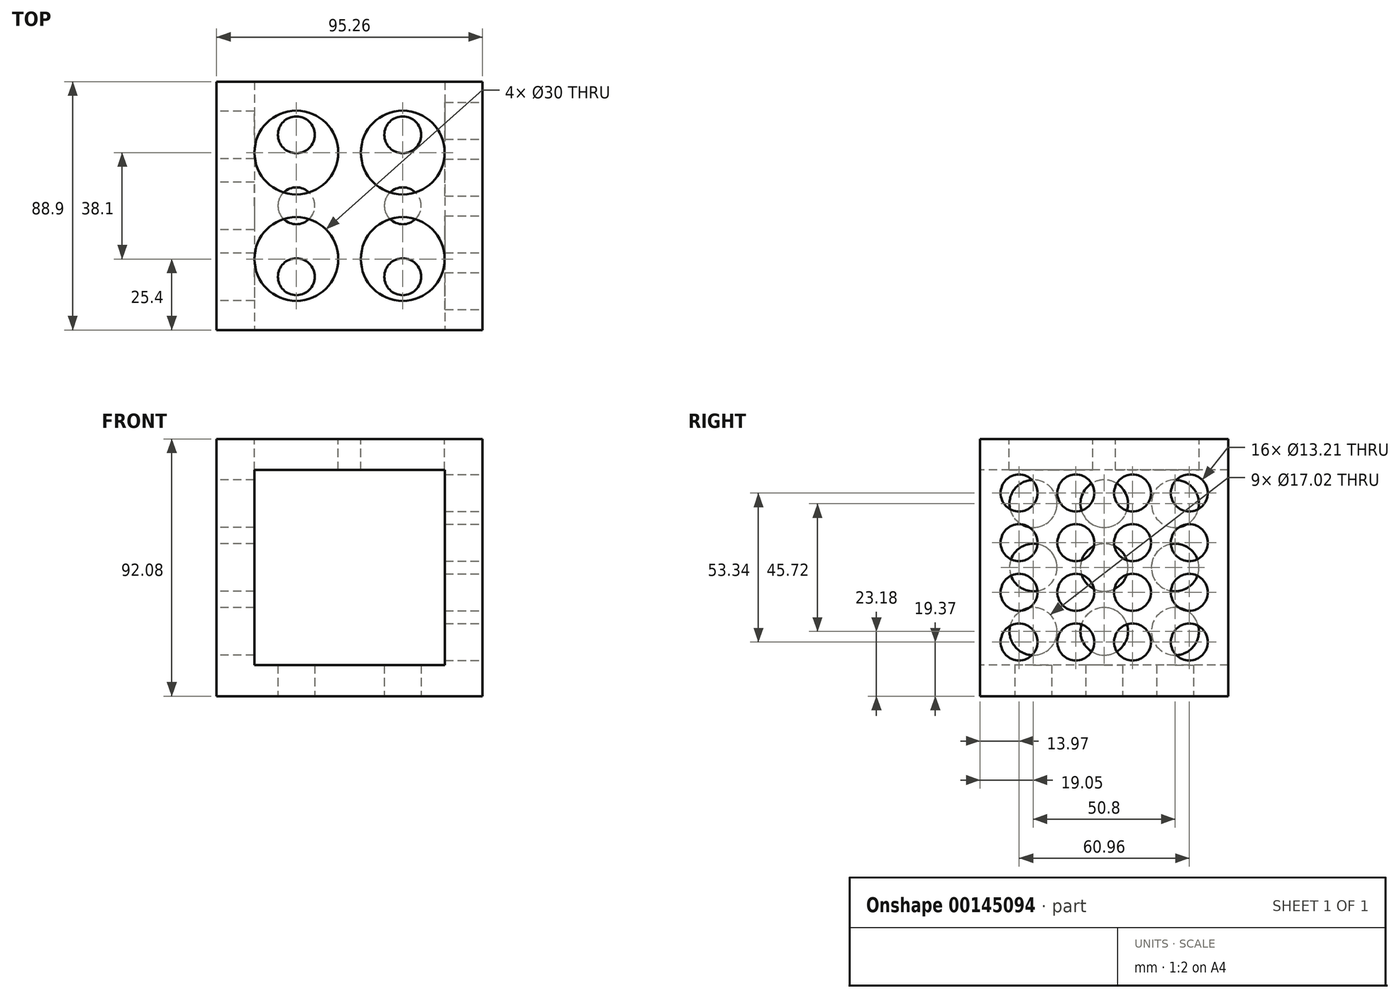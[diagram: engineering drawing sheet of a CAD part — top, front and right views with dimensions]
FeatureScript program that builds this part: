
annotation { "Feature Type Name" : "Feature", "Feature Type Description" : "" }
export const myFeature = defineFeature(function(context is Context, id is Id, definition is map)
    precondition{}
    {
        {
            var Q0;
            Q0=qCreatedBy(makeId("Top.planeOp"),FACE);
            var sketch = newSketch(context, id + "F0", { "sketchPlane" : qUnion([Q0])});
            skLineSegment(sketch, "E0.bottom", {"start": v(47.63, -44.45) * mm, "end": v(-47.62, -44.45) * mm});
            skLineSegment(sketch, "E0.top", {"start": v(47.63, 44.45) * mm, "end": v(-47.62, 44.45) * mm});
            skLineSegment(sketch, "E0.left", {"start": v(47.63, -44.45) * mm, "end": v(47.63, 44.45) * mm});
            skLineSegment(sketch, "E0.right", {"start": v(-47.62, -44.45) * mm, "end": v(-47.62, 44.45) * mm});
            skPoint(sketch, "E0.middle", {"position": v(0, 0) * mm});
            skSolve(sketch);
        }
        {
            var Q0;
            Q0=makeQuery(id+"F0.imprint","IMPRINT",FACE,{"disambiguationData":[TD([[makeQuery(id+"F0.imprint","IMPRINT",EDGE,{"derivedFrom":sQuery(id+"F0.wireOp",EDGE,"E0.bottom")}),-1.0]])]});
            extrude(context, id + "F1", {"entities" : qUnion([Q0]), "depth" : 46.04 * mm, "hasSecondDirection" : true, "secondDirectionOppositeDirection" : true, "secondDirectionDepth" : 46.04 * mm});
        }
        {
            var Q0;
            Q0=makeQuery(id+"F1.opExtrude","SWEPT_FACE",FACE,{"disambiguationData":[OSD([sQuery(id+"F0.wireOp",EDGE,"E0.bottom")])]});
            var sketch = newSketch(context, id + "F2", { "sketchPlane" : qUnion([Q0])});
            skLineSegment(sketch, "E1.bottom", {"start": v(34.13, -34.93) * mm, "end": v(-34.13, -34.93) * mm});
            skLineSegment(sketch, "E1.top", {"start": v(34.13, 34.93) * mm, "end": v(-34.13, 34.92) * mm});
            skLineSegment(sketch, "E1.left", {"start": v(34.13, -34.93) * mm, "end": v(34.13, 34.93) * mm});
            skLineSegment(sketch, "E1.right", {"start": v(-34.13, -34.93) * mm, "end": v(-34.13, 34.92) * mm});
            skPoint(sketch, "E1.middle", {"position": v(0, 0) * mm});
            skLineSegment(sketch, "E2.bottom", {"start": v(1.59, -34.93) * mm, "end": v(-1.59, -34.93) * mm});
            skLineSegment(sketch, "E2.top", {"start": v(1.59, 34.93) * mm, "end": v(-1.59, 34.93) * mm});
            skLineSegment(sketch, "E2.left", {"start": v(1.59, -34.92) * mm, "end": v(1.59, 34.92) * mm});
            skLineSegment(sketch, "E2.right", {"start": v(-1.59, -34.92) * mm, "end": v(-1.59, 34.92) * mm});
            skSolve(sketch);
        }
        {
            var Q0;
            Q0=makeQuery(id+"F2.imprint","IMPRINT",FACE,{"disambiguationData":[TD([[makeQuery(id+"F2.imprint","IMPRINT",EDGE,{"derivedFrom":sQuery(id+"F2.wireOp",EDGE,"E1.bottom")}),-1.0]])]});
            extrude(context, id + "F3", {"entities" : qUnion([Q0]), "operationType" : NewBodyOperationType.REMOVE, "endBound" : BoundingType.UP_TO_NEXT, "oppositeDirection" : true, "depth" : 25.4 * mm});
        }
        {
            var Q0;
            Q0=makeQuery(id+"F1.opExtrude","CAP_FACE",FACE,{"disambiguationData":[OSD([sQuery(id+"F0.wireOp",EDGE,"E0.bottom"),sQuery(id+"F0.wireOp",EDGE,"E0.top"),sQuery(id+"F0.wireOp",EDGE,"E0.left"),sQuery(id+"F0.wireOp",EDGE,"E0.right")])],"isStart":false});
            var sketch = newSketch(context, id + "F4", { "sketchPlane" : qUnion([Q0])});
            skLineSegment(sketch, "E3", {"start": v(0, 0) * mm, "end": v(-19.05, 0) * mm});
            skLineSegment(sketch, "E4", {"start": v(-19.05, 0) * mm, "end": v(-19.05, 19.05) * mm});
            skCircle(sketch, "E5", {"center": v(-19.05, 19.05) * mm, "radius": 15 * mm});
            skLineSegment(sketch, "E6", {"start": v(0, 0) * mm, "end": v(19.05, 0) * mm});
            skLineSegment(sketch, "E7", {"start": v(19.05, 0) * mm, "end": v(19.05, 19.05) * mm});
            skLineSegment(sketch, "E8", {"start": v(-19.05, 0) * mm, "end": v(-19.05, -19.05) * mm});
            skLineSegment(sketch, "E9", {"start": v(19.05, 0) * mm, "end": v(19.05, -19.05) * mm});
            skCircle(sketch, "E10", {"center": v(19.05, 19.05) * mm, "radius": 15 * mm});
            skCircle(sketch, "E11", {"center": v(19.05, -19.05) * mm, "radius": 15 * mm});
            skCircle(sketch, "E12", {"center": v(-19.05, -19.05) * mm, "radius": 15 * mm});
            skSolve(sketch);
        }
        {
            var Q0;
            Q0=makeQuery(id+"F4.imprint","IMPRINT",FACE,{"disambiguationData":[TD([[makeQuery(id+"F4.imprint","IMPRINT",EDGE,{"derivedFrom":sQuery(id+"F4.wireOp",EDGE,"E5")}),1.0]])]});
            var Q1;
            Q1=makeQuery(id+"F4.imprint","IMPRINT",FACE,{"disambiguationData":[TD([[makeQuery(id+"F4.imprint","IMPRINT",EDGE,{"derivedFrom":sQuery(id+"F4.wireOp",EDGE,"E10")}),1.0]])]});
            var Q2;
            Q2=makeQuery(id+"F4.imprint","IMPRINT",FACE,{"disambiguationData":[TD([[makeQuery(id+"F4.imprint","IMPRINT",EDGE,{"derivedFrom":sQuery(id+"F4.wireOp",EDGE,"E11")}),1.0]])]});
            var Q3;
            Q3=makeQuery(id+"F4.imprint","IMPRINT",FACE,{"disambiguationData":[TD([[makeQuery(id+"F4.imprint","IMPRINT",EDGE,{"derivedFrom":sQuery(id+"F4.wireOp",EDGE,"E12")}),1.0]])]});
            extrude(context, id + "F5", {"entities" : qUnion([Q0, Q1, Q2, Q3]), "operationType" : NewBodyOperationType.REMOVE, "endBound" : BoundingType.UP_TO_NEXT, "oppositeDirection" : true, "depth" : 25.4 * mm});
        }
        {
            var Q0;
            Q0=makeQuery(id+"F1.opExtrude","SWEPT_FACE",FACE,{"disambiguationData":[OSD([sQuery(id+"F0.wireOp",EDGE,"E0.right")])]});
            var sketch = newSketch(context, id + "F6", { "sketchPlane" : qUnion([Q0])});
            skCircle(sketch, "E13", {"center": v(0, 0) * mm, "radius": 8.5 * mm});
            skLineSegment(sketch, "E14", {"start": v(0, 0) * mm, "end": v(0, 22.86) * mm});
            skLineSegment(sketch, "E15", {"start": v(0, 0) * mm, "end": v(0, -22.86) * mm});
            skCircle(sketch, "E16", {"center": v(0, 22.86) * mm, "radius": 8.5 * mm});
            skCircle(sketch, "E17", {"center": v(0, -22.86) * mm, "radius": 8.5 * mm});
            skCircle(sketch, "E18.1.0.0", {"center": v(-25.4, 22.86) * mm, "radius": 8.5 * mm});
            skCircle(sketch, "E18.1.0.1", {"center": v(-25.4, 0) * mm, "radius": 8.5 * mm});
            skCircle(sketch, "E18.1.0.2", {"center": v(-25.4, -22.86) * mm, "radius": 8.5 * mm});
            skLineSegment(sketch, "E18.direction1", {"start": v(0, 22.86) * mm, "end": v(-25.4, 22.86) * mm, "construction": true});
            skCircle(sketch, "E19.1.0.0", {"center": v(25.4, 22.86) * mm, "radius": 8.5 * mm});
            skCircle(sketch, "E19.1.0.1", {"center": v(25.4, 0) * mm, "radius": 8.5 * mm});
            skCircle(sketch, "E19.1.0.2", {"center": v(25.4, -22.86) * mm, "radius": 8.5 * mm});
            skLineSegment(sketch, "E19.direction1", {"start": v(0, 22.86) * mm, "end": v(25.4, 22.86) * mm, "construction": true});
            skSolve(sketch);
        }
        {
            var Q0;
            Q0 = qSketchRegion(id + "F6", true);
            extrude(context, id + "F7", {"entities" : qUnion([Q0]), "operationType" : NewBodyOperationType.REMOVE, "endBound" : BoundingType.UP_TO_NEXT, "oppositeDirection" : true, "depth" : 25.4 * mm});
        }
        {
            var Q0;
            Q0=makeQuery(id+"F1.opExtrude","CAP_FACE",FACE,{"disambiguationData":[OSD([sQuery(id+"F0.wireOp",EDGE,"E0.bottom"),sQuery(id+"F0.wireOp",EDGE,"E0.top"),sQuery(id+"F0.wireOp",EDGE,"E0.left"),sQuery(id+"F0.wireOp",EDGE,"E0.right")])],"isStart":true});
            var sketch = newSketch(context, id + "F8", { "sketchPlane" : qUnion([Q0])});
            skLineSegment(sketch, "E20", {"start": v(0, 0) * mm, "end": v(-19.05, 0) * mm});
            skPoint(sketch, "E20.endSnap0", {"position": v(-47.62, 0) * mm});
            skCircle(sketch, "E21", {"center": v(-19.05, 0) * mm, "radius": 6.6 * mm});
            skLineSegment(sketch, "E22", {"start": v(-19.05, 0) * mm, "end": v(-19.05, 25.4) * mm});
            skLineSegment(sketch, "E23", {"start": v(-19.05, 0) * mm, "end": v(-19.05, -25.4) * mm});
            skCircle(sketch, "E24", {"center": v(-19.05, 25.4) * mm, "radius": 6.6 * mm});
            skCircle(sketch, "E25", {"center": v(-19.05, -25.4) * mm, "radius": 6.6 * mm});
            skCircle(sketch, "E26.1.0.0", {"center": v(19.05, 25.4) * mm, "radius": 6.6 * mm});
            skLineSegment(sketch, "E26.1.0.1", {"start": v(19.05, 0) * mm, "end": v(19.05, 25.4) * mm});
            skCircle(sketch, "E26.1.0.2", {"center": v(19.05, 0) * mm, "radius": 6.6 * mm});
            skCircle(sketch, "E26.1.0.3", {"center": v(19.05, -25.4) * mm, "radius": 6.6 * mm});
            skLineSegment(sketch, "E26.direction1", {"start": v(-19.05, 25.4) * mm, "end": v(19.05, 25.4) * mm, "construction": true});
            skSolve(sketch);
        }
        {
            var Q0;
            Q0 = qSketchRegion(id + "F8", true);
            extrude(context, id + "F9", {"entities" : qUnion([Q0]), "operationType" : NewBodyOperationType.REMOVE, "endBound" : BoundingType.UP_TO_NEXT, "oppositeDirection" : true, "depth" : 25.4 * mm});
        }
        {
            var Q0;
            Q0=makeQuery(id+"F1.opExtrude","SWEPT_FACE",FACE,{"disambiguationData":[OSD([sQuery(id+"F0.wireOp",EDGE,"E0.left")])]});
            var sketch = newSketch(context, id + "F10", { "sketchPlane" : qUnion([Q0])});
            skLineSegment(sketch, "E27", {"start": v(0, 0) * mm, "end": v(-30.48, 0) * mm});
            skLineSegment(sketch, "E28", {"start": v(-30.48, 0) * mm, "end": v(-30.48, 8.89) * mm});
            skLineSegment(sketch, "E29", {"start": v(-30.48, 8.89) * mm, "end": v(-30.48, 26.67) * mm});
            skCircle(sketch, "E30", {"center": v(-30.48, 8.89) * mm, "radius": 6.6 * mm});
            skCircle(sketch, "E31", {"center": v(-30.48, 26.67) * mm, "radius": 6.6 * mm});
            skCircle(sketch, "E32.MirrorC", {"center": v(-30.48, -8.89) * mm, "radius": 6.6 * mm});
            skLineSegment(sketch, "E33.MirrorCS", {"start": v(-30.48, -8.89) * mm, "end": v(-30.48, -26.67) * mm});
            skLineSegment(sketch, "E34.MirrorCS", {"start": v(-30.48, 0) * mm, "end": v(-30.48, -8.89) * mm});
            skCircle(sketch, "E35.MirrorC", {"center": v(-30.48, -26.67) * mm, "radius": 6.6 * mm});
            skCircle(sketch, "E36.1.0.0", {"center": v(-10.16, 26.67) * mm, "radius": 6.6 * mm});
            skLineSegment(sketch, "E36.1.0.1", {"start": v(-10.16, 8.89) * mm, "end": v(-10.16, 26.67) * mm});
            skCircle(sketch, "E36.1.0.2", {"center": v(-10.16, 8.89) * mm, "radius": 6.6 * mm});
            skLineSegment(sketch, "E36.1.0.3", {"start": v(-10.16, 0) * mm, "end": v(-10.16, -8.89) * mm});
            skLineSegment(sketch, "E36.1.0.4", {"start": v(-10.16, 0) * mm, "end": v(-10.16, 8.89) * mm});
            skCircle(sketch, "E36.1.0.5", {"center": v(-10.16, -8.89) * mm, "radius": 6.6 * mm});
            skLineSegment(sketch, "E36.1.0.6", {"start": v(-10.16, -8.89) * mm, "end": v(-10.16, -26.67) * mm});
            skCircle(sketch, "E36.1.0.7", {"center": v(-10.16, -26.67) * mm, "radius": 6.6 * mm});
            skCircle(sketch, "E36.2.0.0", {"center": v(10.16, 26.67) * mm, "radius": 6.6 * mm});
            skLineSegment(sketch, "E36.2.0.1", {"start": v(10.16, 8.89) * mm, "end": v(10.16, 26.67) * mm});
            skCircle(sketch, "E36.2.0.2", {"center": v(10.16, 8.89) * mm, "radius": 6.6 * mm});
            skLineSegment(sketch, "E36.2.0.3", {"start": v(10.16, 0) * mm, "end": v(10.16, -8.89) * mm});
            skLineSegment(sketch, "E36.2.0.4", {"start": v(10.16, 0) * mm, "end": v(10.16, 8.89) * mm});
            skCircle(sketch, "E36.2.0.5", {"center": v(10.16, -8.89) * mm, "radius": 6.6 * mm});
            skLineSegment(sketch, "E36.2.0.6", {"start": v(10.16, -8.89) * mm, "end": v(10.16, -26.67) * mm});
            skCircle(sketch, "E36.2.0.7", {"center": v(10.16, -26.67) * mm, "radius": 6.6 * mm});
            skCircle(sketch, "E36.3.0.0", {"center": v(30.48, 26.67) * mm, "radius": 6.6 * mm});
            skLineSegment(sketch, "E36.3.0.1", {"start": v(30.48, 8.89) * mm, "end": v(30.48, 26.67) * mm});
            skCircle(sketch, "E36.3.0.2", {"center": v(30.48, 8.89) * mm, "radius": 6.6 * mm});
            skLineSegment(sketch, "E36.3.0.3", {"start": v(30.48, 0) * mm, "end": v(30.48, -8.89) * mm});
            skLineSegment(sketch, "E36.3.0.4", {"start": v(30.48, 0) * mm, "end": v(30.48, 8.89) * mm});
            skCircle(sketch, "E36.3.0.5", {"center": v(30.48, -8.89) * mm, "radius": 6.6 * mm});
            skLineSegment(sketch, "E36.3.0.6", {"start": v(30.48, -8.89) * mm, "end": v(30.48, -26.67) * mm});
            skCircle(sketch, "E36.3.0.7", {"center": v(30.48, -26.67) * mm, "radius": 6.6 * mm});
            skLineSegment(sketch, "E36.direction1", {"start": v(-30.48, 26.67) * mm, "end": v(-10.16, 26.67) * mm, "construction": true});
            skSolve(sketch);
        }
        {
            var Q0;
            Q0 = qSketchRegion(id + "F10", true);
            extrude(context, id + "F11", {"entities" : qUnion([Q0]), "operationType" : NewBodyOperationType.REMOVE, "endBound" : BoundingType.UP_TO_NEXT, "oppositeDirection" : true, "depth" : 25.4 * mm});
        }
    });
